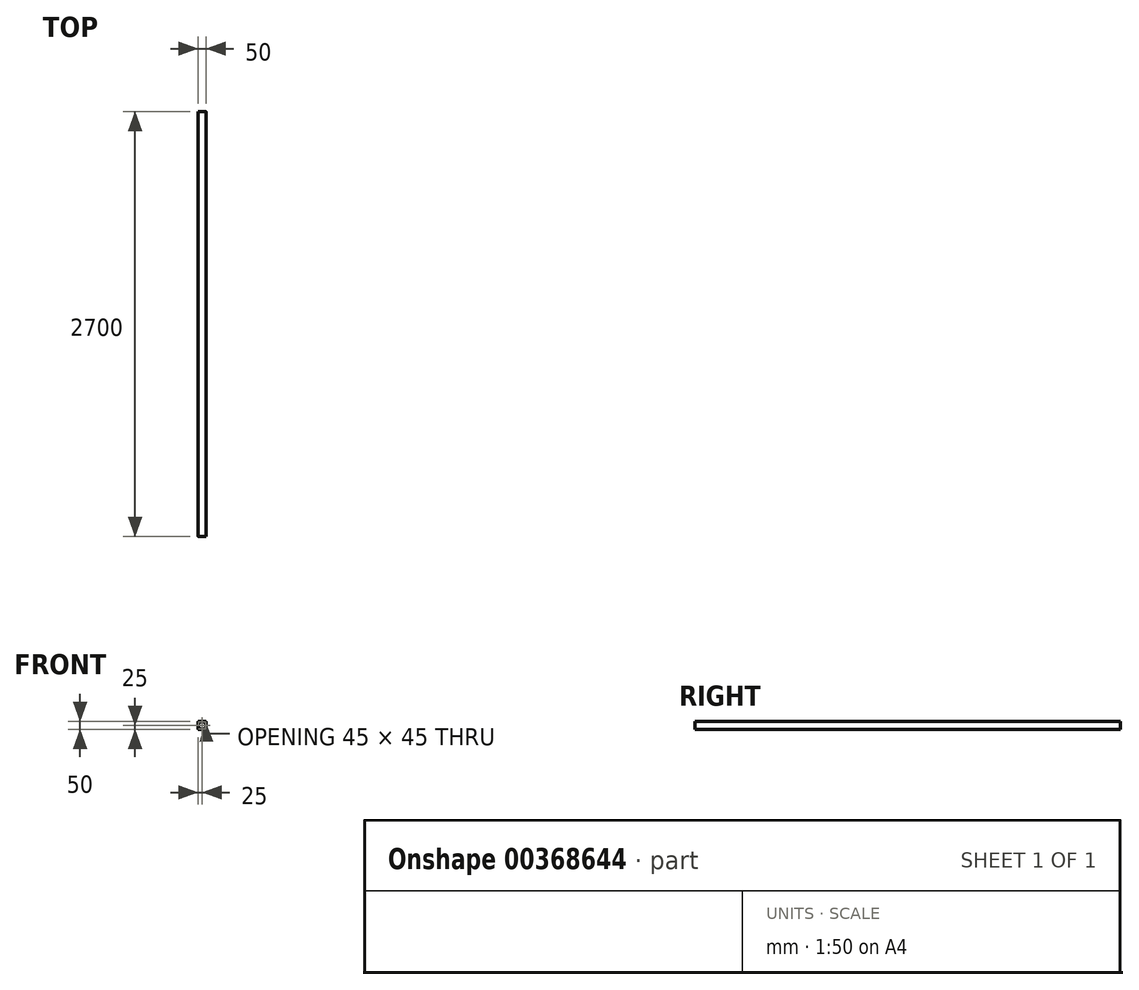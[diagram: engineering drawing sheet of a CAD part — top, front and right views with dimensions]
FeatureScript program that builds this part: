
annotation { "Feature Type Name" : "Feature", "Feature Type Description" : "" }
export const myFeature = defineFeature(function(context is Context, id is Id, definition is map)
    precondition{}
    {
        {
            var Q0;
            Q0=qCreatedBy(makeId("Front.planeOp"),FACE);
            var sketch = newSketch(context, id + "F0", { "sketchPlane" : qUnion([Q0])});
            skLineSegment(sketch, "E0.bottom", {"start": v(23, 25) * mm, "end": v(-23, 25) * mm});
            skLineSegment(sketch, "E0.top", {"start": v(23, -25) * mm, "end": v(-23, -25) * mm});
            skLineSegment(sketch, "E0.left", {"start": v(25, 23) * mm, "end": v(25, -23) * mm});
            skLineSegment(sketch, "E0.right", {"start": v(-25, 23) * mm, "end": v(-25, -23) * mm});
            skPoint(sketch, "E0.middle", {"position": v(0, 0) * mm});
            skLineSegment(sketch, "E1.bottom", {"start": v(20.5, 22.5) * mm, "end": v(-20.5, 22.5) * mm});
            skLineSegment(sketch, "E1.top", {"start": v(20.5, -22.5) * mm, "end": v(-20.5, -22.5) * mm});
            skLineSegment(sketch, "E1.left", {"start": v(22.5, 20.5) * mm, "end": v(22.5, -20.5) * mm});
            skLineSegment(sketch, "E1.right", {"start": v(-22.5, 20.5) * mm, "end": v(-22.5, -20.5) * mm});
            skPoint(sketch, "E2.visualSharp", {"position": v(-25, 25) * mm});
            skArc(sketch, "E2.filletArc", {"start": v(-23, 25) * mm, "mid": v(-24.41, 24.41) * mm, "end": v(-25, 23) * mm});
            skPoint(sketch, "E3.visualSharp", {"position": v(25, 25) * mm});
            skArc(sketch, "E3.filletArc", {"start": v(25, 23) * mm, "mid": v(24.41, 24.41) * mm, "end": v(23, 25) * mm});
            skPoint(sketch, "E4.visualSharp", {"position": v(22.5, 22.5) * mm});
            skArc(sketch, "E4.filletArc", {"start": v(22.5, 20.5) * mm, "mid": v(21.91, 21.91) * mm, "end": v(20.5, 22.5) * mm});
            skPoint(sketch, "E5.visualSharp", {"position": v(-22.5, 22.5) * mm});
            skArc(sketch, "E5.filletArc", {"start": v(-20.5, 22.5) * mm, "mid": v(-21.91, 21.91) * mm, "end": v(-22.5, 20.5) * mm});
            skPoint(sketch, "E6.visualSharp", {"position": v(-22.5, -22.5) * mm});
            skArc(sketch, "E6.filletArc", {"start": v(-22.5, -20.5) * mm, "mid": v(-21.91, -21.91) * mm, "end": v(-20.5, -22.5) * mm});
            skPoint(sketch, "E7.visualSharp", {"position": v(-25, -25) * mm});
            skArc(sketch, "E7.filletArc", {"start": v(-25, -23) * mm, "mid": v(-24.41, -24.41) * mm, "end": v(-23, -25) * mm});
            skPoint(sketch, "E8.visualSharp", {"position": v(22.5, -22.5) * mm});
            skArc(sketch, "E8.filletArc", {"start": v(20.5, -22.5) * mm, "mid": v(21.91, -21.91) * mm, "end": v(22.5, -20.5) * mm});
            skPoint(sketch, "E9.visualSharp", {"position": v(25, -25) * mm});
            skArc(sketch, "E9.filletArc", {"start": v(23, -25) * mm, "mid": v(24.41, -24.41) * mm, "end": v(25, -23) * mm});
            skSolve(sketch);
        }
        {
            var Q0;
            Q0=qSketchRegion(id+"F0",true);
            extrude(context, id + "F1", {"entities" : qUnion([Q0]), "endBound" : BoundingType.SYMMETRIC, "depth" : 2700 * mm});
        }
    });
